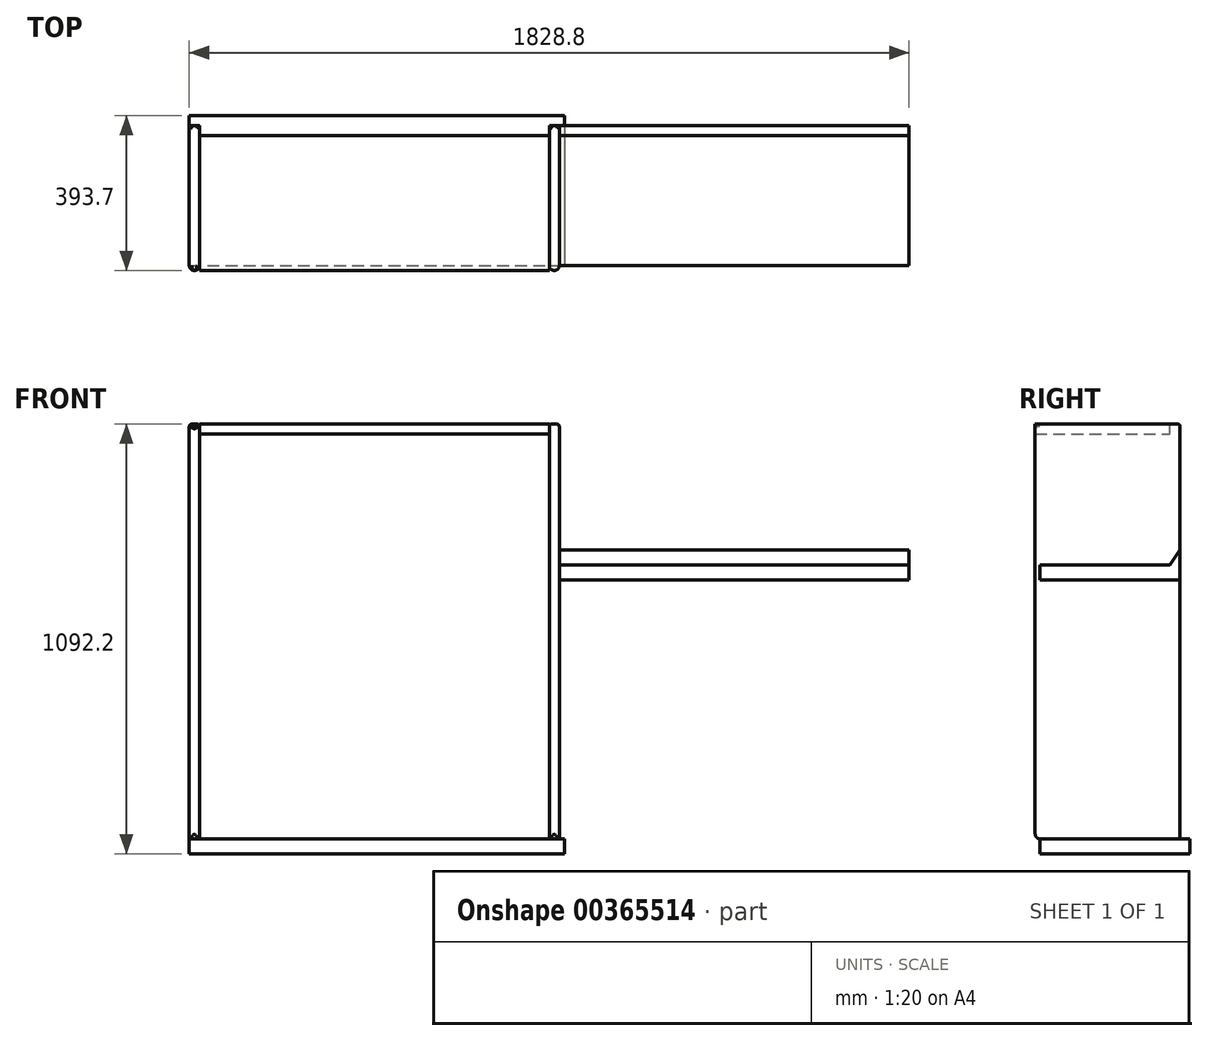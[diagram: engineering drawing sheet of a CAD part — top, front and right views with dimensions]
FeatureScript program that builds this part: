
annotation { "Feature Type Name" : "Feature", "Feature Type Description" : "" }
export const myFeature = defineFeature(function(context is Context, id is Id, definition is map)
    precondition{}
    {
        {
            var Q0;
            Q0=qCreatedBy(makeId("Right.planeOp"),FACE);
            var sketch = newSketch(context, id + "F0", { "sketchPlane" : qUnion([Q0])});
            skLineSegment(sketch, "E0", {"start": v(0, 0) * mm, "end": v(368.3, 0) * mm});
            skLineSegment(sketch, "E1", {"start": v(0, 0) * mm, "end": v(0, -1054.1) * mm});
            skLineSegment(sketch, "E2", {"start": v(0, -1054.1) * mm, "end": v(368.3, -1054.1) * mm});
            skLineSegment(sketch, "E3", {"start": v(368.3, -1054.1) * mm, "end": v(368.3, 0) * mm});
            skSolve(sketch);
        }
        {
            var Q0;
            Q0=qSketchRegion(id+"F0",true);
            extrude(context, id + "F1", {"entities" : qUnion([Q0]), "depth" : 25.4 * mm});
        }
        {
            var Q0;
            Q0=makeQuery(id+"F1.opExtrude","SWEPT_FACE",FACE,{"disambiguationData":[OSD([sQuery(id+"F0.wireOp",EDGE,"E0")])]});
            fillet(context, id + "F2", {"entities" : qUnion([Q0]), "radius" : 6.35 * mm, "tangentPropagation" : true, "allowEdgeOverflow" : false});
        }
        {
            var Q0;
            Q0=makeQuery(id+"F1.opExtrude","SWEPT_FACE",FACE,{"disambiguationData":[OSD([sQuery(id+"F0.wireOp",EDGE,"E1")])]});
            fillet(context, id + "F3", {"entities" : qUnion([Q0]), "radius" : 12.7 * mm, "tangentPropagation" : true, "allowEdgeOverflow" : false});
        }
        {
            var Q0;
            Q0=qCreatedBy(makeId("Top.planeOp"),FACE);
            var sketch = newSketch(context, id + "F4", { "sketchPlane" : qUnion([Q0])});
            skLineSegment(sketch, "E4.bottom", {"start": v(0, 0) * mm, "end": v(-889, 0) * mm});
            skLineSegment(sketch, "E4.top", {"start": v(0, 342.9) * mm, "end": v(-889, 342.9) * mm});
            skLineSegment(sketch, "E4.left", {"start": v(0, 0) * mm, "end": v(0, 342.9) * mm});
            skLineSegment(sketch, "E4.right", {"start": v(-889, 0) * mm, "end": v(-889, 342.9) * mm});
            skSolve(sketch);
        }
        {
            var Q0;
            Q0=makeQuery(id+"F4.imprint","IMPRINT",FACE,{"disambiguationData":[TD([[makeQuery(id+"F4.imprint","IMPRINT",EDGE,{"derivedFrom":sQuery(id+"F4.wireOp",EDGE,"E4.bottom")}),-1.0]])]});
            extrude(context, id + "F5", {"entities" : qUnion([Q0]), "oppositeDirection" : true, "depth" : 25.4 * mm});
        }
        {
            var Q0;
            Q0=makeQuery(id+"F5.opExtrude","SWEPT_FACE",FACE,{"disambiguationData":[OSD([sQuery(id+"F4.wireOp",EDGE,"E4.right")])]});
            var sketch = newSketch(context, id + "F6", { "sketchPlane" : qUnion([Q0])});
            skLineSegment(sketch, "E5", {"start": v(0, 0) * mm, "end": v(0, -1054.1) * mm});
            skLineSegment(sketch, "E6", {"start": v(0, -1054.1) * mm, "end": v(-368.3, -1054.1) * mm});
            skLineSegment(sketch, "E7", {"start": v(0, 0) * mm, "end": v(-368.3, 0) * mm});
            skLineSegment(sketch, "E8", {"start": v(-368.3, 0) * mm, "end": v(-368.3, -1054.1) * mm});
            skSolve(sketch);
        }
        {
            var Q0;
            Q0=qSketchRegion(id+"F6",true);
            extrude(context, id + "F7", {"entities" : qUnion([Q0]), "depth" : 25.4 * mm});
        }
        {
            var Q0;
            Q0=makeQuery(id+"F7.opExtrude","SWEPT_FACE",FACE,{"disambiguationData":[OSD([sQuery(id+"F6.wireOp",EDGE,"E5")])]});
            fillet(context, id + "F8", {"entities" : qUnion([Q0]), "radius" : 12.7 * mm, "tangentPropagation" : true, "allowEdgeOverflow" : false});
        }
        {
            var Q0;
            Q0=makeQuery(id+"F7.opExtrude","SWEPT_FACE",FACE,{"disambiguationData":[OSD([sQuery(id+"F6.wireOp",EDGE,"E7")])]});
            fillet(context, id + "F9", {"entities" : qUnion([Q0]), "radius" : 6.35 * mm, "tangentPropagation" : true, "allowEdgeOverflow" : false});
        }
        {
            var Q0;
            Q0=makeQuery(id+"F1.opExtrude","CAP_FACE",FACE,{"disambiguationData":[OSD([sQuery(id+"F0.wireOp",EDGE,"E0"),sQuery(id+"F0.wireOp",EDGE,"E1"),sQuery(id+"F0.wireOp",EDGE,"E2"),sQuery(id+"F0.wireOp",EDGE,"E3")])],"isStart":false});
            var sketch = newSketch(context, id + "F10", { "sketchPlane" : qUnion([Q0])});
            skLineSegment(sketch, "E9", {"start": v(368.3, -320.04) * mm, "end": v(368.3, -396.24) * mm});
            skLineSegment(sketch, "E10", {"start": v(368.3, -396.24) * mm, "end": v(12.7, -396.24) * mm});
            skLineSegment(sketch, "E11", {"start": v(12.7, -396.24) * mm, "end": v(12.7, -358.14) * mm});
            skPoint(sketch, "E11.endSnap0", {"position": v(368.3, -358.14) * mm});
            skLineSegment(sketch, "E12", {"start": v(12.7, -358.14) * mm, "end": v(342.9, -358.14) * mm});
            skLineSegment(sketch, "E13", {"start": v(342.9, -358.14) * mm, "end": v(368.3, -320.04) * mm});
            skSolve(sketch);
        }
        {
            var Q0;
            Q0=qSketchRegion(id+"F10",true);
            extrude(context, id + "F11", {"entities" : qUnion([Q0]), "depth" : 889 * mm});
        }
        {
            var Q0;
            Q0=makeQuery(id+"F7.opExtrude","SWEPT_FACE",FACE,{"disambiguationData":[OSD([sQuery(id+"F6.wireOp",EDGE,"E6")])]});
            var sketch = newSketch(context, id + "F12", { "sketchPlane" : qUnion([Q0])});
            skLineSegment(sketch, "E14", {"start": v(-914.4, -12.7) * mm, "end": v(-914.4, -393.7) * mm});
            skLineSegment(sketch, "E15", {"start": v(-914.4, -393.7) * mm, "end": v(38.1, -393.7) * mm});
            skLineSegment(sketch, "E16", {"start": v(38.1, -393.7) * mm, "end": v(38.1, -12.7) * mm});
            skLineSegment(sketch, "E17", {"start": v(38.1, -12.7) * mm, "end": v(-914.4, -12.7) * mm});
            skSolve(sketch);
        }
        {
            var Q0;
            Q0=qSketchRegion(id+"F12",true);
            extrude(context, id + "F13", {"entities" : qUnion([Q0]), "depth" : 38.1 * mm});
        }
    });
